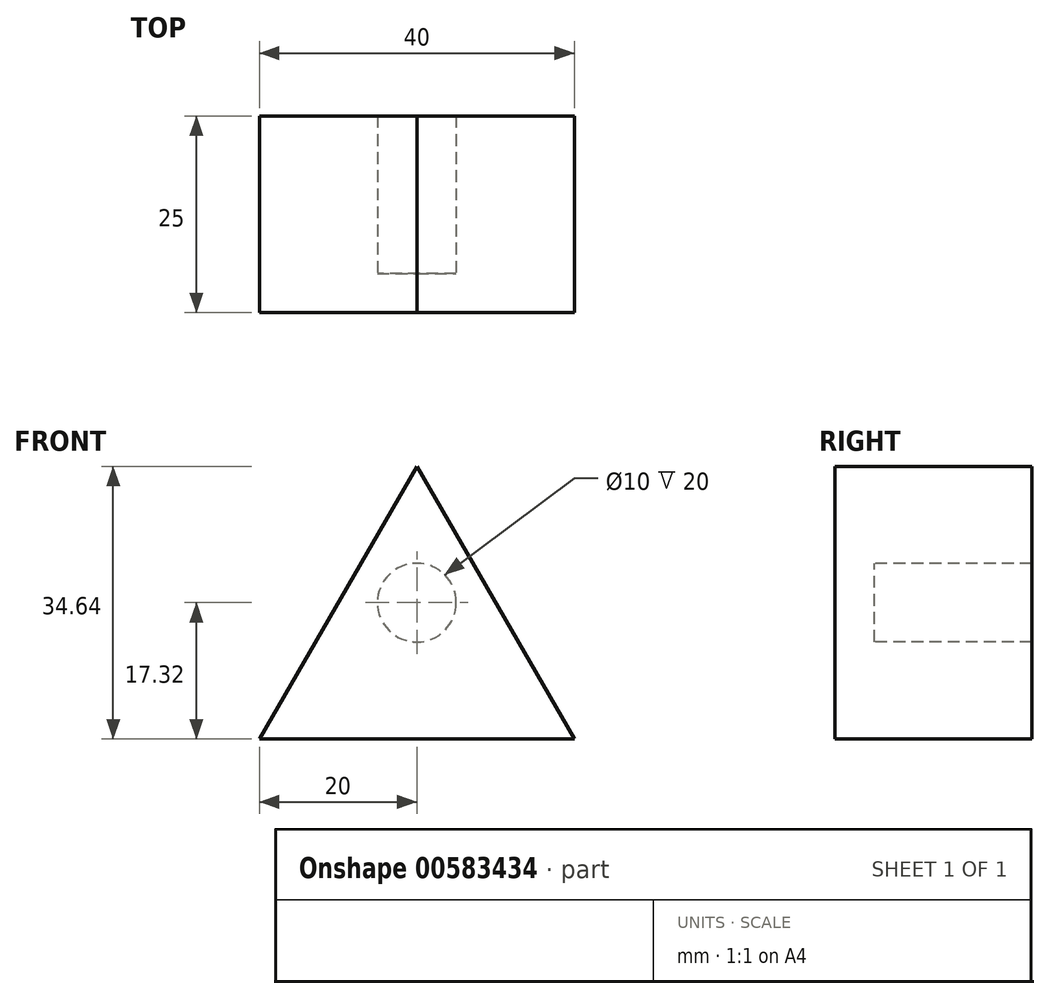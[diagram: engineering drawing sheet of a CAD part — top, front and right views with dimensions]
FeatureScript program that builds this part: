
annotation { "Feature Type Name" : "Feature", "Feature Type Description" : "" }
export const myFeature = defineFeature(function(context is Context, id is Id, definition is map)
    precondition{}
    {
        {
            var Q0;
            Q0=qCreatedBy(makeId("Front.planeOp"),FACE);
            var sketch = newSketch(context, id + "F0", { "sketchPlane" : qUnion([Q0])});
            skLineSegment(sketch, "E0", {"start": v(0, 0) * mm, "end": v(-20, 0) * mm});
            skLineSegment(sketch, "E1", {"start": v(0, 0) * mm, "end": v(20, 0) * mm});
            skLineSegment(sketch, "E2", {"start": v(-20, 0) * mm, "end": v(0, 34.64) * mm});
            skLineSegment(sketch, "E3", {"start": v(0, 34.64) * mm, "end": v(20, 0) * mm});
            skSolve(sketch);
        }
        {
            var Q0;
            Q0=makeQuery(id+"F0.imprint","IMPRINT",FACE,{"disambiguationData":[TD([[makeQuery(id+"F0.imprint","IMPRINT",EDGE,{"derivedFrom":sQuery(id+"F0.wireOp",EDGE,"E0")}),-1.0]])]});
            extrude(context, id + "F1", {"entities" : qUnion([Q0]), "depth" : 5 * mm, "offsetDistance" : 25 * mm});
        }
        {
            var Q0;
            Q0=makeQuery(id+"F1.opExtrude","CAP_FACE",FACE,{"disambiguationData":[OSD([sQuery(id+"F0.wireOp",EDGE,"E0"),sQuery(id+"F0.wireOp",EDGE,"E1"),sQuery(id+"F0.wireOp",EDGE,"E2"),sQuery(id+"F0.wireOp",EDGE,"E3")])],"isStart":false});
            var sketch = newSketch(context, id + "F2", { "sketchPlane" : qUnion([Q0])});
            skLineSegment(sketch, "E4", {"start": v(0, 0) * mm, "end": v(0, 34.64) * mm});
            skCircle(sketch, "E5", {"center": v(0, 17.32) * mm, "radius": 5 * mm});
            skSolve(sketch);
        }
        {
            var Q0;
            {var subQ0=sQuery(id+"F2.wireOp",EDGE,"E5");var subQ1=sQuery(id+"F2.wireOp",EDGE,"E4");var subQ2=makeQuery(id+"F2.imprint","INTERSECT",VERTEX,{"disambiguationData":[OD(0.0)],"derivedFrom":[subQ1,subQ0]});Q0=makeQuery(id+"F2.imprint","IMPRINT",FACE,{"disambiguationData":[TD([[makeQuery(id+"F2.imprint","IMPRINT",EDGE,{"disambiguationData":[TD([[subQ2,-1.0]])],"derivedFrom":subQ1}),-1.0]])]});}
            var Q1;
            {var subQ0=sQuery(id+"F2.wireOp",EDGE,"E5");var subQ1=sQuery(id+"F2.wireOp",EDGE,"E4");var subQ2=makeQuery(id+"F2.imprint","INTERSECT",VERTEX,{"disambiguationData":[OD(0.0)],"derivedFrom":[subQ1,subQ0]});Q1=makeQuery(id+"F2.imprint","IMPRINT",FACE,{"disambiguationData":[TD([[makeQuery(id+"F2.imprint","IMPRINT",EDGE,{"disambiguationData":[TD([[subQ2,-1.0]])],"derivedFrom":subQ1}),1.0]])]});}
            extrude(context, id + "F3", {"entities" : qUnion([Q0, Q1]), "operationType" : NewBodyOperationType.ADD, "oppositeDirection" : true, "depth" : 25 * mm, "offsetDistance" : 25 * mm});
        }
    });
